# Revit family: RN 40210 Rubinetto da giardino antigelo
name_source: partatom
category: Rohrzubehör
units: mm (PartAtom-declared; Revit-internal decimal feet)

## family parameters
Arbeitsebenenbasiert = Nein
Beim Laden mit Abzugskörper schneiden = Nein
Bemaßung runder Anschluss = Durchmesser verwenden
Gemeinsam genutzt = Nein
Immer vertikal = Ja
Teiletyp = Ventil - Zerlegung in

## types (2) — shared parameters
1.010.00.2 Blattnummer der Richtlinie = 17
1.010.00.3 Ausgabedatum (Monat) der Richtlinie = 201601
1.010.00.4 Herstellername = R. Nussbaum AG
1.010.00.5 Revisionsdatum der Datei = 20190528
1.010.00.6 Webadresse des Herstellers = http://www.nussbaum.ch
1.100.00.3 Sortiernummer für Anzeigereihenfolge = 3
1.100.00.4 Produktbezeichnung = Entnahmearmaturen
1.960/3L.00.8 Link (URL) = https://www.nussbaum.ch
17.700.00.4 Armaturentyp = 4
17.700.00.5 Nennweite DN = 20
17.700.00.6 kvs-Wert [m3/h] = 1.86
17.700.00.7 Maximale Betriebstemperatur TB [°C] = 90
17.700.00.8 Maximaler Betriebsdruck (Arbeitsdruck) ps [1.0 · 105 Pa] = 16
CONNECTOR0_DIAMETER_dZ_0r = 20 mm
CONNECTOR0_dZ_00 = 21 mm
CONNECTOR0_dZ_01 = 31 mm
CONNECTOR0_ref_dZ = 31 mm
CONNECTOR1_DIAMETER_dZ_0r = 15 mm
CONNECTOR1_dZ_00 = 31 mm
CONNECTOR1_dZ_01 = 21 mm
CONNECTOR1_ref_dZ = 21 mm
Connector Visibility = Nein
EnclosingSpace Visibility = Nein
Hersteller = R. Nussbauzm AG
URL = https://www.nussbaum.ch

## per-type parameters (varying)
| type | 1.800.00.3 TGA-Nummer | 1.810.00.3 Hersteller-Bestellnummer | 1.810.00.4 DATANORM-Nummer | 1.810.00.5 StLB-Nummer | 1.810.00.6 GTIN-Nummer | 17.700.00.30 Produktbeschreibung | CONNECTOR1_ref_dX | Modell | R. Nussbaum AG 40210.71 de Visibility | R. Nussbaum AG 40210.72 de Visibility | Typenkommentare |
| DN 20 | 00301000000000000000000000000200200000000000000001???00000 | 40210.71 | 40210.71 | 633.434 | 7612945701633 | 40210.71, Gartenventil frostsicher, mit Umsteller und Steckschlüssel, DN=20 | 412 mm | 40210.71 | Ja | Nein | Rubinetto da giardino antigeloDN 20 |
| DN 20 1 | 00301000000000000000000000000200200000000000000002???00000 | 40210.72 | 40210.72 | 633.444 | 7612945701640 | 40210.72, Gartenventil frostsicher, mit Umsteller und Steckschlüssel, DN=20 | 617 mm | 40210.72 | Nein | Ja | Rubinetto da giardino antigeloDN 20 1 |

## geometry (parser evidence)
native form markers: Sweep x2
no freeform markers — native parametric forms only
